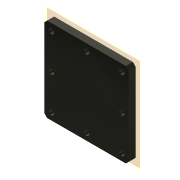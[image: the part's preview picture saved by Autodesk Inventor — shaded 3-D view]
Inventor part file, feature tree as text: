
AUTODESK INVENTOR PART (.ipt)
format: ipt  version: 2022 (Build 260153000, 153)  size: 112,128 bytes
history: native  units: mm
features: other x4, reference x3, sketch x2, plane x1, extrude x1, hole x1
ambient origin geometry x8: Origin, YZ Plane, XZ Plane, XY Plane, X Axis, Y Axis, Z Axis, Center Point
bodies: Solid1 (feature_tree)
feature tree (12):
  plane  "Work Plane1"
  extrude  "Extrusion1"  Depth=50.0mm
  hole  "Hole1"  [1 undecoded]
  sketch  "Sketch1"  dims[d0=50.0mm d1=50.0mm]
  reference  "Reference1"
  sketch  "Sketch2"  dims[d2=6.0mm d3=0.0mm d4=50.0mm d5=50.0mm d6=3.9mm d7=6.0mm d8=4.0mm d9=2.0mm d10=90.0deg d11=10.0mm d12=20.594885mm]
  reference  "Reference2"
  reference  "Reference3"
  other  "00_XY_stage-CHUO_SEIKI_LD-647-R1.iam"
  other  "00_XY_stage-CHUO_SEIKI_LD-647-R1-Middle:1"
  other  "00_XY_stage-CHUO_SEIKI_LD-647-R1-Top:1"
  other  "Assembly2"
note: 1 required parameter value undecoded (feature->parameter linkage not recoverable at this tier; creation-order binding heuristic only, values carry confidence <= 0.55)
